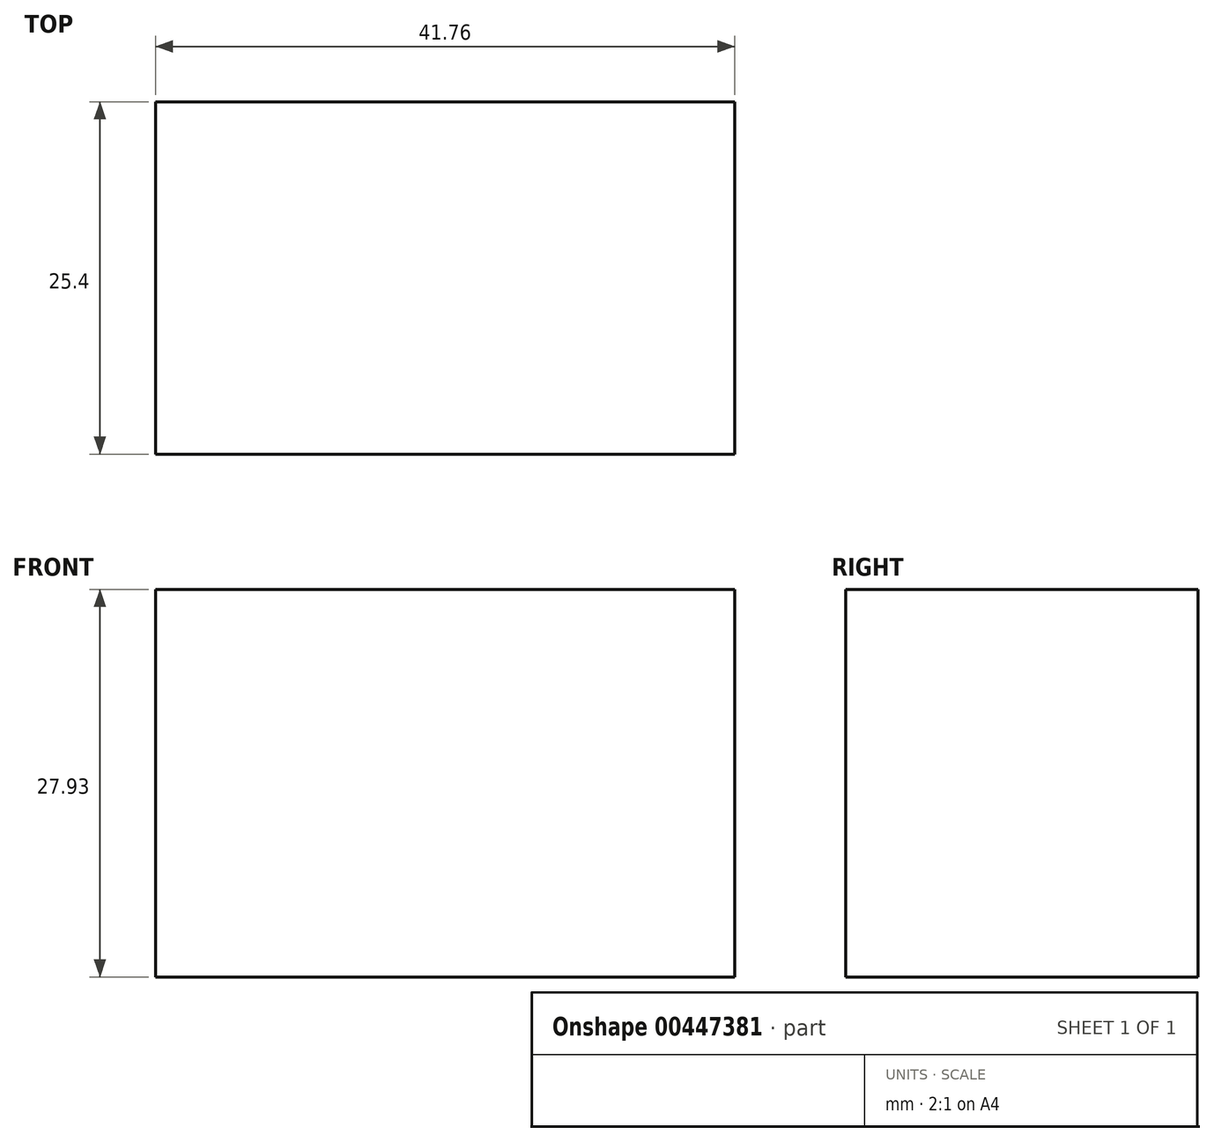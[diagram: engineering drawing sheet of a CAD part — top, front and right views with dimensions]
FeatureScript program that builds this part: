
annotation { "Feature Type Name" : "Feature", "Feature Type Description" : "" }
export const myFeature = defineFeature(function(context is Context, id is Id, definition is map)
    precondition{}
    {
        {
            var Q0;
            Q0=qCreatedBy(makeId("Front.planeOp"),FACE);
            var sketch = newSketch(context, id + "F0", { "sketchPlane" : qUnion([Q0])});
            skLineSegment(sketch, "E0.bottom", {"start": v(0, 0) * mm, "end": v(41.76, 0) * mm});
            skLineSegment(sketch, "E0.top", {"start": v(0, 27.93) * mm, "end": v(41.76, 27.93) * mm});
            skLineSegment(sketch, "E0.left", {"start": v(0, 0) * mm, "end": v(0, 27.93) * mm});
            skLineSegment(sketch, "E0.right", {"start": v(41.76, 0) * mm, "end": v(41.76, 27.93) * mm});
            skSolve(sketch);
        }
        {
            var Q0;
            Q0=makeQuery(id+"F0.imprint","IMPRINT",FACE,{"disambiguationData":[TD([[makeQuery(id+"F0.imprint","IMPRINT",EDGE,{"derivedFrom":sQuery(id+"F0.wireOp",EDGE,"E0.bottom")}),1.0]])]});
            extrude(context, id + "F1", {"entities" : qUnion([Q0]), "depth" : 25.4 * mm});
        }
    });
